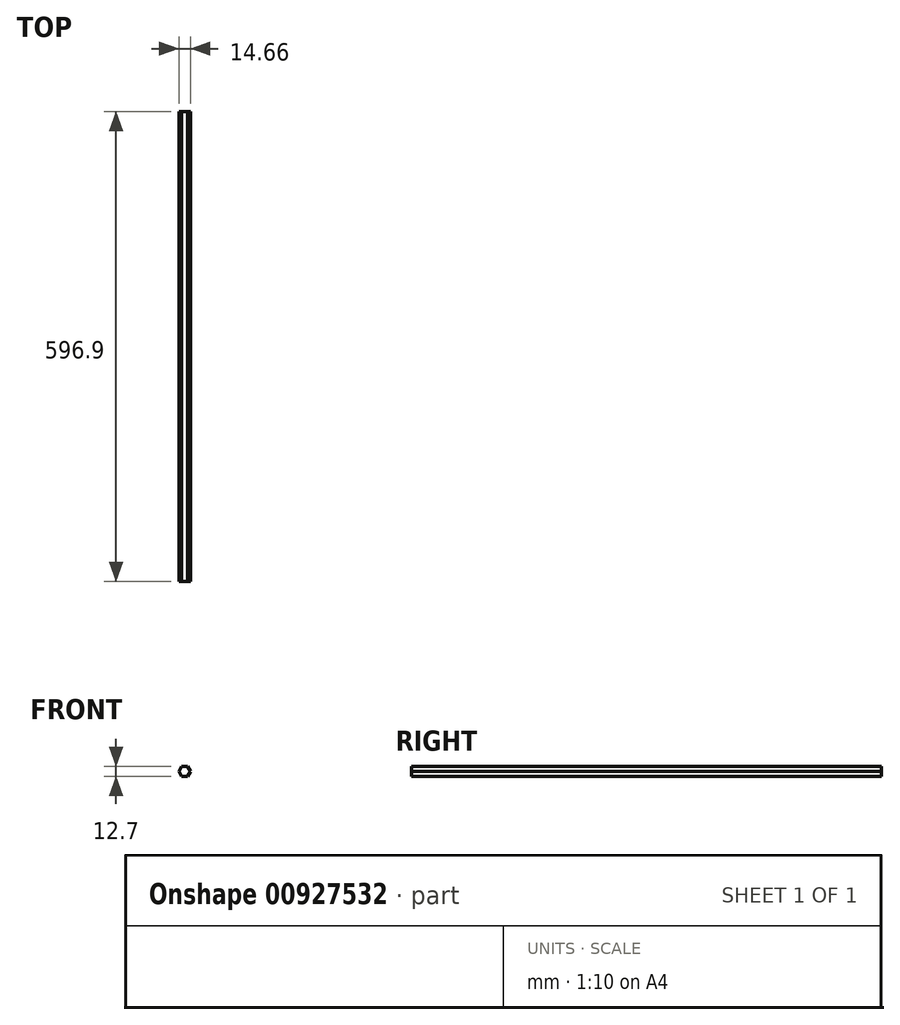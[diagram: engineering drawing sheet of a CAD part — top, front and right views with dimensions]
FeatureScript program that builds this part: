
annotation { "Feature Type Name" : "Feature", "Feature Type Description" : "" }
export const myFeature = defineFeature(function(context is Context, id is Id, definition is map)
    precondition{}
    {
        {
            var Q0;
            Q0=qCreatedBy(makeId("Front.planeOp"),FACE);
            var sketch = newSketch(context, id + "F0", { "sketchPlane" : qUnion([Q0])});
            skCircle(sketch, "E0.cCircle", {"center": v(0, 0) * mm, "radius": 6.35 * mm, "construction": true});
            skLineSegment(sketch, "E0.0", {"start": v(-3.67, 6.35) * mm, "end": v(3.67, 6.35) * mm});
            skLineSegment(sketch, "E0.1", {"start": v(3.67, 6.35) * mm, "end": v(7.33, 0) * mm});
            skLineSegment(sketch, "E0.2", {"start": v(7.33, 0) * mm, "end": v(3.67, -6.35) * mm});
            skLineSegment(sketch, "E0.3", {"start": v(3.67, -6.35) * mm, "end": v(-3.67, -6.35) * mm});
            skLineSegment(sketch, "E0.4", {"start": v(-3.67, -6.35) * mm, "end": v(-7.33, 0) * mm});
            skLineSegment(sketch, "E0.5", {"start": v(-7.33, 0) * mm, "end": v(-3.67, 6.35) * mm});
            skPoint(sketch, "E0.0.midPoint", {"position": v(0, 6.35) * mm});
            skSolve(sketch);
        }
        {
            var Q0;
            Q0=qSketchRegion(id+"F0",true);
            var Q1;
            Q1=makeQuery(id+"F0.imprint","IMPRINT",FACE,{"disambiguationData":[TD([[makeQuery(id+"F0.imprint","IMPRINT",EDGE,{"derivedFrom":sQuery(id+"F0.wireOp",EDGE,"E0.0")}),-1.0]])]});
            extrude(context, id + "F1", {"entities" : qUnion([Q0, Q1]), "depth" : 596.9 * mm, "offsetDistance" : 25.4 * mm});
        }
    });
